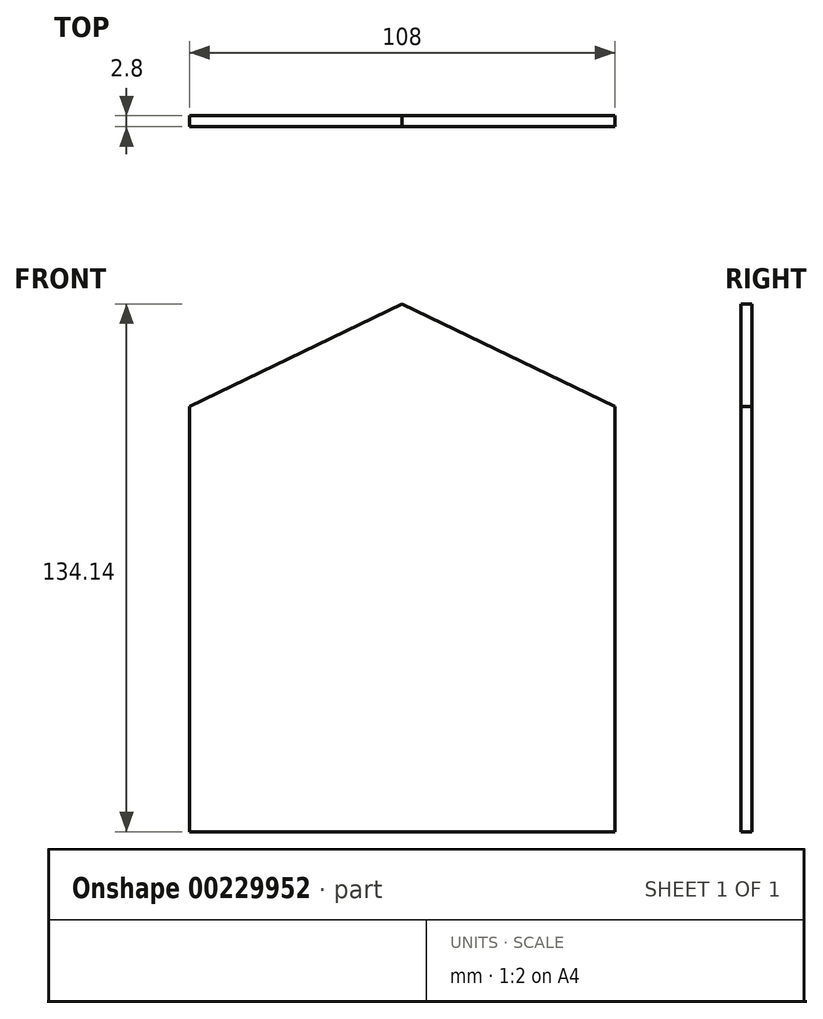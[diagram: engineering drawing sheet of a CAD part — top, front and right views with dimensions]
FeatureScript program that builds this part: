
annotation { "Feature Type Name" : "Feature", "Feature Type Description" : "" }
export const myFeature = defineFeature(function(context is Context, id is Id, definition is map)
    precondition{}
    {
        {
            var Q0;
            Q0=qCreatedBy(makeId("Front.planeOp"),FACE);
            var sketch = newSketch(context, id + "F0", { "sketchPlane" : qUnion([Q0])});
            skLineSegment(sketch, "E0.bottom", {"start": v(-54, 54) * mm, "end": v(54, 54) * mm});
            skLineSegment(sketch, "E0.top", {"start": v(-54, -54) * mm, "end": v(54, -54) * mm});
            skLineSegment(sketch, "E0.left", {"start": v(-54, 54) * mm, "end": v(-54, -54) * mm});
            skLineSegment(sketch, "E0.right", {"start": v(54, 54) * mm, "end": v(54, -54) * mm});
            skPoint(sketch, "E0.middle", {"position": v(0, 0) * mm});
            skLineSegment(sketch, "E1", {"start": v(-54, 54) * mm, "end": v(0, 80.14) * mm});
            skLineSegment(sketch, "E2", {"start": v(0, 80.14) * mm, "end": v(54, 54) * mm});
            skSolve(sketch);
        }
        {
            var Q0;
            Q0 = qSketchRegion(id + "F0", true);
            extrude(context, id + "F1", {"entities" : qUnion([Q0]), "depth" : 2.8 * mm});
        }
    });
